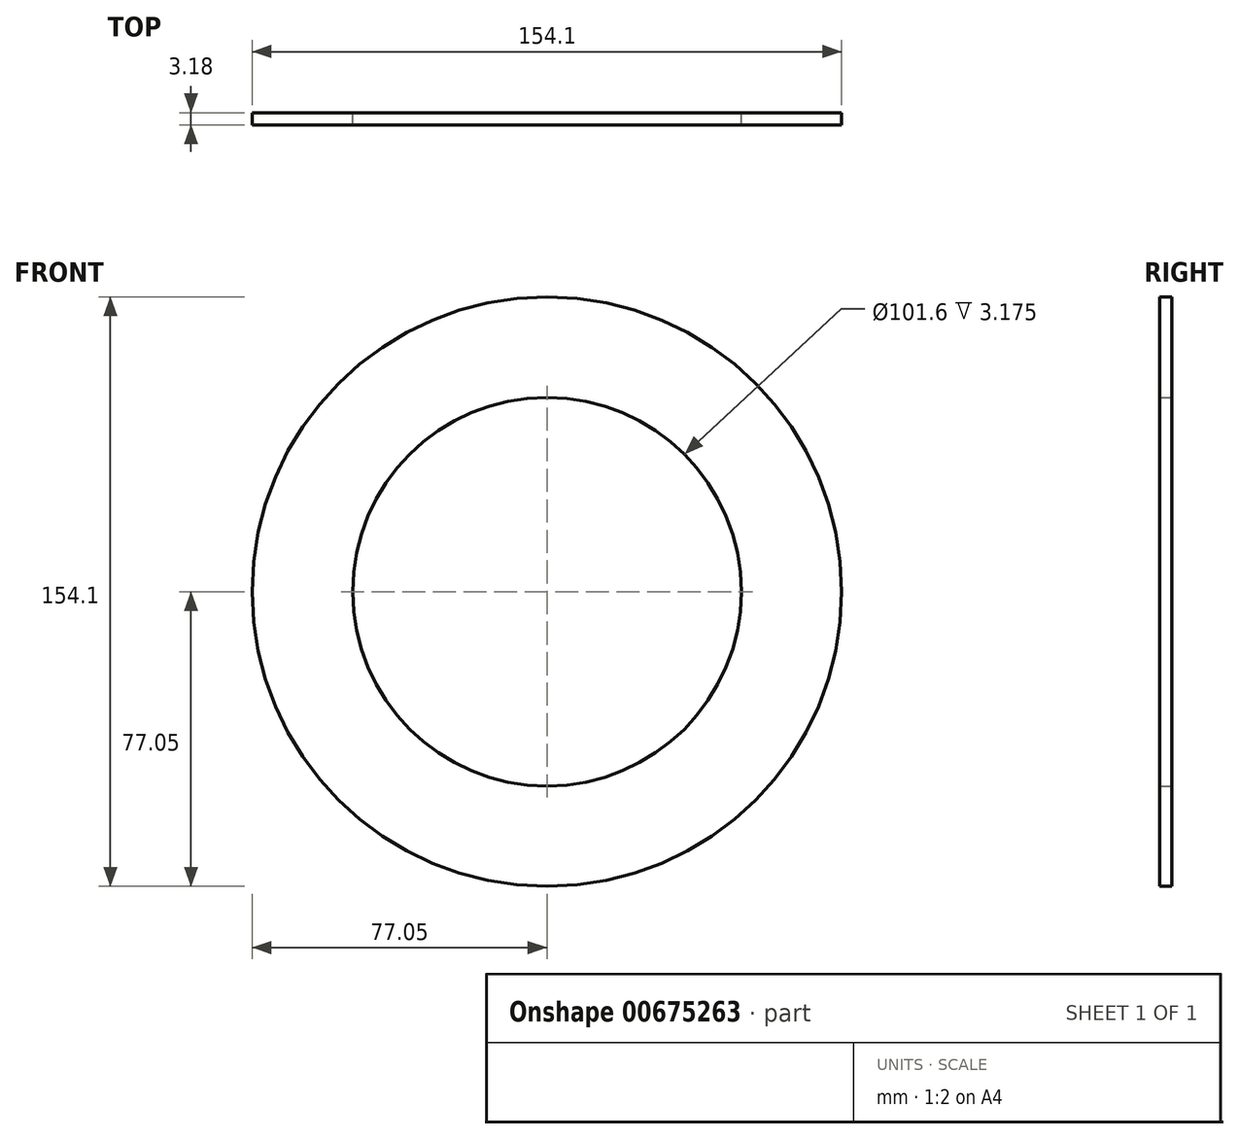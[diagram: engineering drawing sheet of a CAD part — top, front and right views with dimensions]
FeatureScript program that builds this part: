
annotation { "Feature Type Name" : "Feature", "Feature Type Description" : "" }
export const myFeature = defineFeature(function(context is Context, id is Id, definition is map)
    precondition{}
    {
        {
            var Q0;
            Q0=qCreatedBy(makeId("Front.planeOp"),FACE);
            var sketch = newSketch(context, id + "F0", { "sketchPlane" : qUnion([Q0])});
            skCircle(sketch, "E0", {"center": v(0, 0) * mm, "radius": 77.05 * mm});
            skCircle(sketch, "E1", {"center": v(0, 0) * mm, "radius": 50.8 * mm});
            skSolve(sketch);
        }
        {
            var Q0;
            Q0 = qSketchRegion(id + "F0", true);
            extrude(context, id + "F1", {"entities" : qUnion([Q0]), "depth" : 3.17 * mm, "offsetDistance" : 25.4 * mm});
        }
    });
